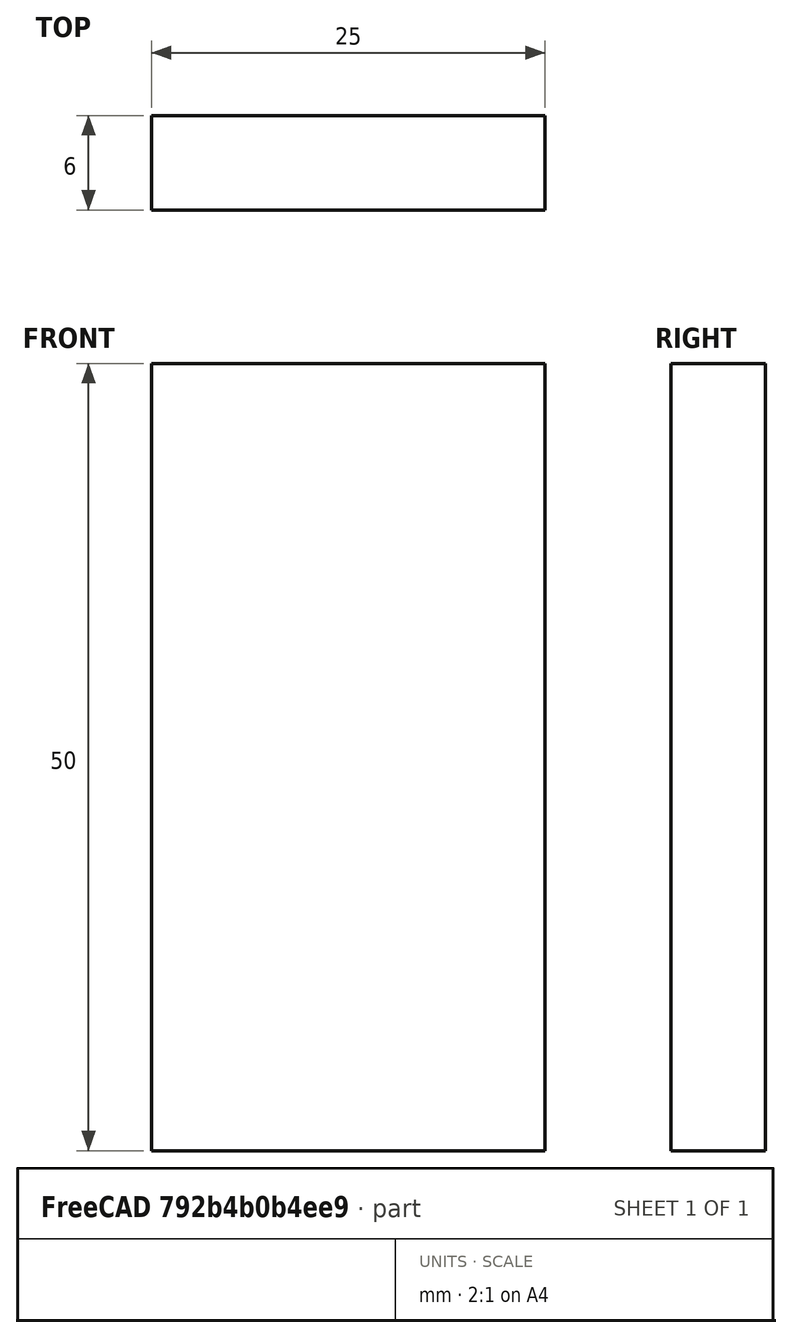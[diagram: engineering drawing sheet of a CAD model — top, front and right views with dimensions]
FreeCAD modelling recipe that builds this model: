
FCSTD DOCUMENT  (FreeCAD 0.15R4671 (Git))
Label: Flat Bar 25x6 EN10058 S235JR
License: All rights reserved
LicenseURL: http://en.wikipedia.org/wiki/All_rights_reserved
objects: Sketcher::SketchObject×1, Part::Extrusion×1
note: 2 computed .brp shape members not serialized (recipe doc carries the construction recipe); baked Part::Feature solids carry a one-line shape summary decoded from their .brp

FEATURE [Sketcher::SketchObject] Sketch
  sketch-geometry (4):
    g0: LineSegment StartX=-12.5 StartY=-3 StartZ=0 EndX=12.5 EndY=-3 EndZ=0
    g1: LineSegment StartX=12.5 StartY=-3 StartZ=0 EndX=12.5 EndY=3 EndZ=0
    g2: LineSegment StartX=12.5 StartY=3 StartZ=0 EndX=-12.5 EndY=3 EndZ=0
    g3: LineSegment StartX=-12.5 StartY=3 StartZ=0 EndX=-12.5 EndY=-3 EndZ=0
  constraints (12):
    c: Coincident(g0,g1)
    c: Coincident(g1,g2)
    c: Coincident(g2,g3)
    c: Coincident(g3,g0)
    c: Horizontal(g0)
    c: Horizontal(g2)
    c: Vertical(g1)
    c: Vertical(g3)
    c: Symmetric(g1,g2,g-2)
    c: Symmetric(g0,g1,g-1)
    c: DistanceY(g1) = 6
    c: DistanceX(g0) = 25
FEATURE [Part::Extrusion] Extrude  label="Flat Bar 25x6 EN10058 S235JR"
  Base = -> Sketch
  Dir = (0,0,50)
  Solid = true
